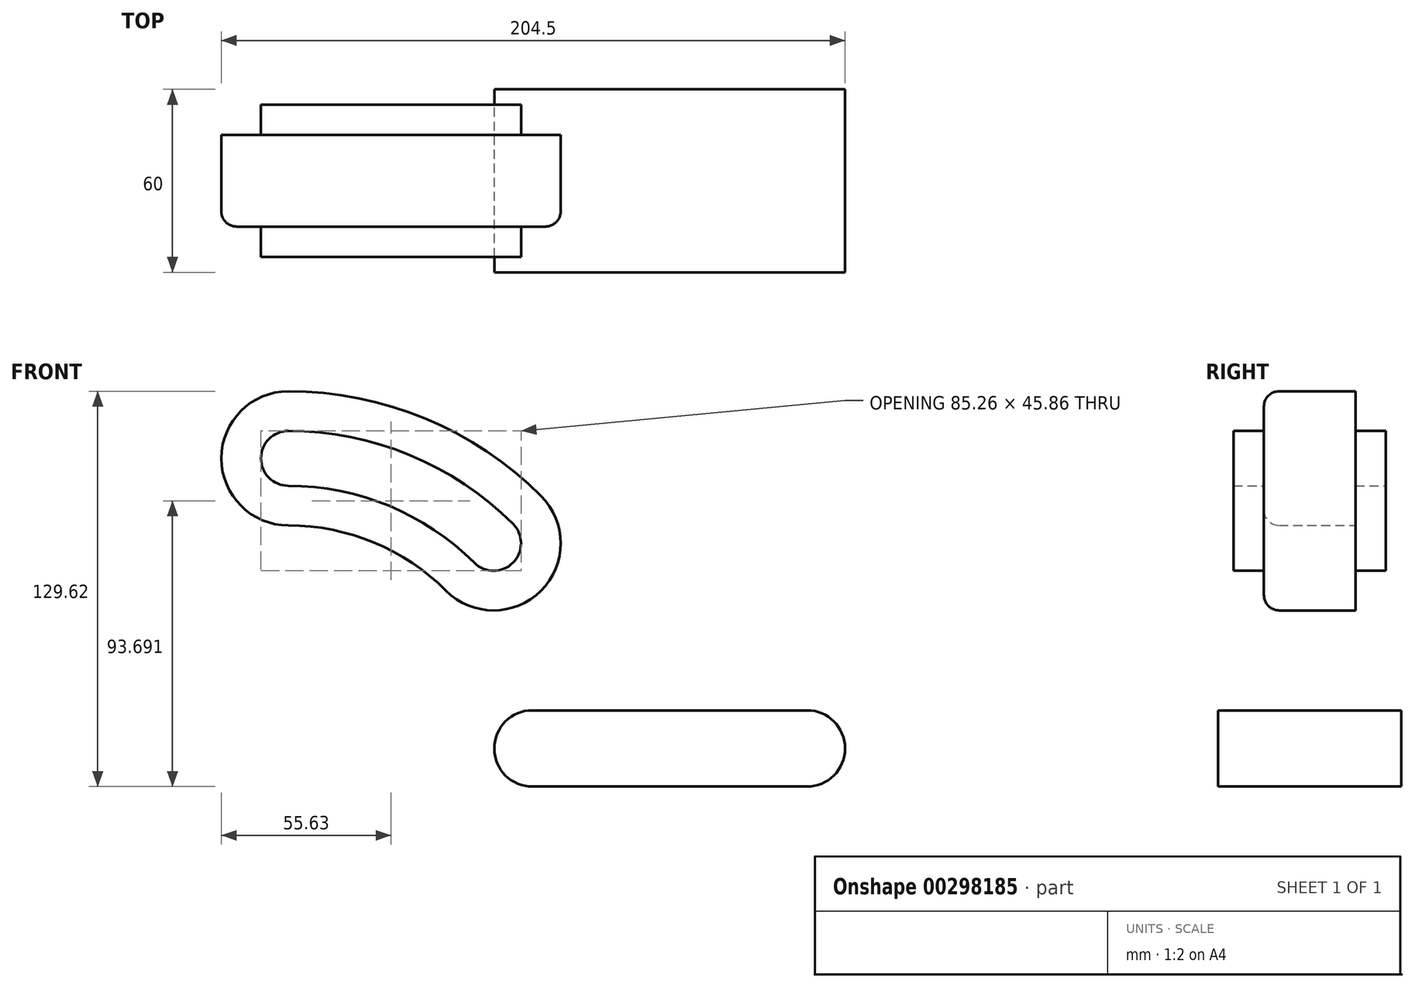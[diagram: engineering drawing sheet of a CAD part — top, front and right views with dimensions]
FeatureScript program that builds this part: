
annotation { "Feature Type Name" : "Feature", "Feature Type Description" : "" }
export const myFeature = defineFeature(function(context is Context, id is Id, definition is map)
    precondition{}
    {
        {
            var Q0;
            Q0=qCreatedBy(makeId("Front.planeOp"),FACE);
            var sketch = newSketch(context, id + "F0", { "sketchPlane" : qUnion([Q0])});
            skArc(sketch, "E0", {"start": v(-8.99, 94.7) * mm, "mid": v(36.4, 87.88) * mm, "end": v(73.32, 60.6) * mm, "construction": true});
            skArc(sketch, "E1.0.startCap", {"start": v(0, 86.12) * mm, "mid": v(-9, 95.12) * mm, "end": v(0, 104.12) * mm});
            skArc(sketch, "E1.0.endCap", {"start": v(73.62, 73.62) * mm, "mid": v(73.62, 60.9) * mm, "end": v(60.9, 60.9) * mm});
            skArc(sketch, "E1.0.left", {"start": v(0, 104.12) * mm, "mid": v(39.85, 96.2) * mm, "end": v(73.62, 73.62) * mm});
            skArc(sketch, "E1.0.right", {"start": v(0, 86.12) * mm, "mid": v(32.96, 79.57) * mm, "end": v(60.9, 60.9) * mm});
            skArc(sketch, "E2.0.startCap", {"start": v(0, 73.12) * mm, "mid": v(-22, 95.12) * mm, "end": v(0, 117.12) * mm});
            skArc(sketch, "E2.0.endCap", {"start": v(82.82, 82.82) * mm, "mid": v(82.82, 51.7) * mm, "end": v(51.7, 51.7) * mm});
            skArc(sketch, "E2.0.left", {"start": v(0, 117.12) * mm, "mid": v(44.82, 108.2) * mm, "end": v(82.82, 82.82) * mm});
            skArc(sketch, "E2.0.right", {"start": v(0, 73.12) * mm, "mid": v(27.98, 67.55) * mm, "end": v(51.7, 51.7) * mm});
            skLineSegment(sketch, "E3", {"start": v(0, 0) * mm, "end": v(170, 0) * mm, "construction": true});
            skArc(sketch, "E4.0.endCap", {"start": v(170, 12.5) * mm, "mid": v(182.5, 0) * mm, "end": v(170, -12.5) * mm});
            skLineSegment(sketch, "E4.0.left", {"start": v(80, 12.5) * mm, "end": v(170, 12.5) * mm});
            skLineSegment(sketch, "E4.0.right", {"start": v(80, -12.5) * mm, "end": v(170, -12.5) * mm});
            skArc(sketch, "E5.0.endCap", {"start": v(170, 25) * mm, "mid": v(195, 0) * mm, "end": v(170, -25) * mm});
            skLineSegment(sketch, "E5.0.left", {"start": v(77.71, 25) * mm, "end": v(170, 25) * mm});
            skLineSegment(sketch, "E5.0.right", {"start": v(77.71, -25) * mm, "end": v(170, -25) * mm});
            skCircle(sketch, "E6", {"center": v(0, 0) * mm, "radius": 40 * mm});
            skArc(sketch, "E7", {"start": v(41.73, 40.28) * mm, "mid": v(-58, 0) * mm, "end": v(41.73, -40.28) * mm});
            skArc(sketch, "E8", {"start": v(41.73, 40.28) * mm, "mid": v(58.17, 28.98) * mm, "end": v(77.71, 25) * mm});
            skArc(sketch, "E9", {"start": v(41.73, -40.28) * mm, "mid": v(58.17, -28.98) * mm, "end": v(77.71, -25) * mm});
            skArc(sketch, "E10", {"start": v(80, 12.5) * mm, "mid": v(67.5, 0) * mm, "end": v(80, -12.5) * mm});
            skLineSegment(sketch, "E11", {"start": v(0, 0) * mm, "end": v(0, 95.12) * mm, "construction": true});
            skLineSegment(sketch, "E12", {"start": v(0, 0) * mm, "end": v(67.26, 67.26) * mm, "construction": true});
            skArc(sketch, "E13", {"start": v(-22, 53.67) * mm, "mid": v(-12.13, 65.39) * mm, "end": v(-16.14, 80.17) * mm});
            skPoint(sketch, "E13.startSnap0", {"position": v(-22, 95.12) * mm});
            skLineSegment(sketch, "E14", {"start": v(63.47, 98.43) * mm, "end": v(183.55, 21.01) * mm});
            skSolve(sketch);
        }
        {
            var Q0;
            Q0=makeQuery(id+"F0.imprint","IMPRINT",FACE,{"disambiguationData":[TD([[makeQuery(id+"F0.imprint","IMPRINT",EDGE,{"derivedFrom":sQuery(id+"F0.wireOp",EDGE,"E4.0.endCap")}),1.0]])]});
            extrude(context, id + "F1", {"entities" : qUnion([Q0]), "endBound" : BoundingType.SYMMETRIC, "depth" : 60 * mm});
        }
        {
            var Q0;
            Q0=makeQuery(id+"F0.imprint","IMPRINT",FACE,{"disambiguationData":[TD([[makeQuery(id+"F0.imprint","IMPRINT",EDGE,{"derivedFrom":sQuery(id+"F0.wireOp",EDGE,"E1.0.startCap")}),1.0]])]});
            extrude(context, id + "F2", {"entities" : qUnion([Q0]), "endBound" : BoundingType.SYMMETRIC, "depth" : 50 * mm});
        }
        {
            var Q0;
            {var subQ1=sQuery(id+"F0.wireOp",EDGE,"E2.0.endCap");Q0=makeQuery(id+"F0.imprint","IMPRINT",FACE,{"disambiguationData":[TD([[makeQuery(id+"F0.imprint","IMPRINT",EDGE,{"derivedFrom":subQ1}),1.0]])]});}
            extrude(context, id + "F3", {"entities" : qUnion([Q0]), "operationType" : NewBodyOperationType.ADD, "endBound" : BoundingType.SYMMETRIC, "depth" : 30 * mm});
        }
        {
            var Q0;
            Q0=makeQuery(id+"F3.opExtrude","CAP_EDGE",EDGE,{"disambiguationData":[OSD([sQuery(id+"F0.wireOp",EDGE,"E14")])],"isStart":false});
            var Q1;
            Q1=makeQuery(id+"F3.opExtrude","CAP_EDGE",EDGE,{"disambiguationData":[OSD([sQuery(id+"F0.wireOp",EDGE,"E2.0.endCap")])],"isStart":false});
            var Q2;
            Q2=makeQuery(id+"F3.opExtrude","CAP_EDGE",EDGE,{"disambiguationData":[OSD([sQuery(id+"F0.wireOp",EDGE,"E2.0.left")])],"isStart":false});
            var Q3;
            Q3=makeQuery(id+"F3.opExtrude","CAP_EDGE",EDGE,{"disambiguationData":[OSD([sQuery(id+"F0.wireOp",EDGE,"E7")])],"isStart":false});
            var Q4;
            Q4=makeQuery(id+"F3.opExtrude","CAP_EDGE",EDGE,{"disambiguationData":[OSD([sQuery(id+"F0.wireOp",EDGE,"E5.0.left")])],"isStart":false});
            var Q5;
            Q5=makeQuery(id+"F3.opExtrude","CAP_EDGE",EDGE,{"disambiguationData":[OSD([sQuery(id+"F0.wireOp",EDGE,"E8")])],"isStart":false});
            var Q6;
            Q6=makeQuery(id+"F3.opExtrude","CAP_EDGE",EDGE,{"disambiguationData":[OSD([sQuery(id+"F0.wireOp",EDGE,"E5.0.endCap")])],"isStart":false});
            fillet(context, id + "F4", {"entities" : qUnion([Q0, Q1, Q2, Q3, Q4, Q5, Q6]), "radius" : 5 * mm, "tangentPropagation" : true, "allowEdgeOverflow" : false});
        }
    });
